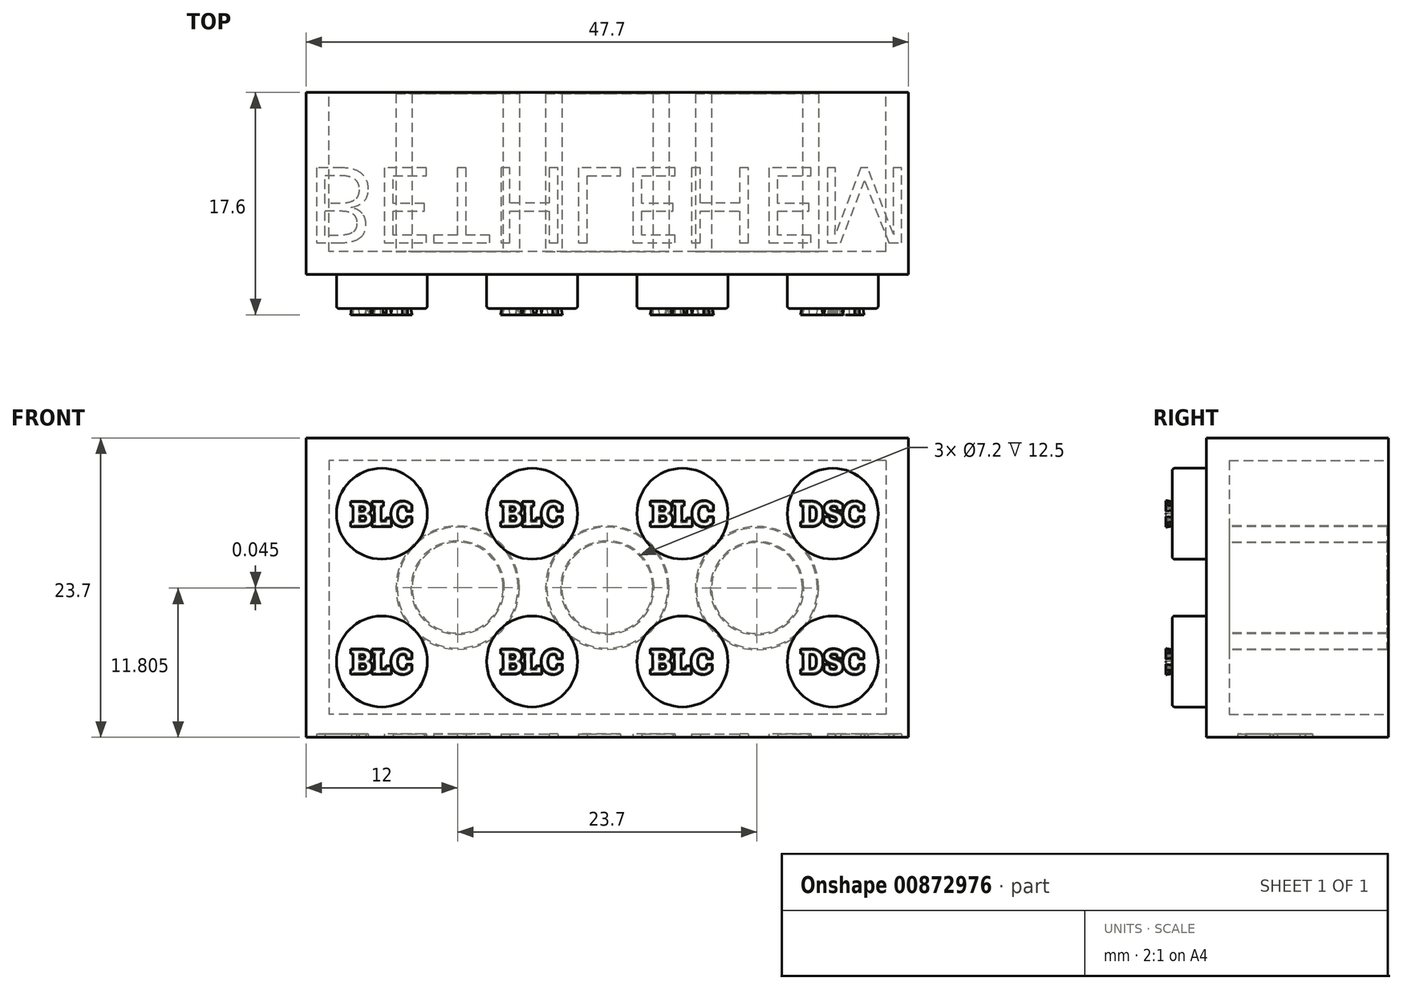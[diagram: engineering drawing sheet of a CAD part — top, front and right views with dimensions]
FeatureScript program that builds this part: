
annotation { "Feature Type Name" : "Feature", "Feature Type Description" : "" }
export const myFeature = defineFeature(function(context is Context, id is Id, definition is map)
    precondition{}
    {
        {
            var Q0;
            Q0=qCreatedBy(makeId("Front.planeOp"),FACE);
            var sketch = newSketch(context, id + "F0", { "sketchPlane" : qUnion([Q0])});
            skLineSegment(sketch, "E0.bottom", {"start": v(-23.85, 11.85) * mm, "end": v(23.85, 11.85) * mm});
            skLineSegment(sketch, "E0.top", {"start": v(-23.85, -11.85) * mm, "end": v(23.85, -11.85) * mm});
            skLineSegment(sketch, "E0.left", {"start": v(-23.85, 11.85) * mm, "end": v(-23.85, -11.85) * mm});
            skLineSegment(sketch, "E0.right", {"start": v(23.85, 11.85) * mm, "end": v(23.85, -11.85) * mm});
            skSolve(sketch);
        }
        {
            var Q0;
            Q0=makeQuery(id+"F0.imprint","IMPRINT",FACE,{"disambiguationData":[TD([[makeQuery(id+"F0.imprint","IMPRINT",EDGE,{"derivedFrom":sQuery(id+"F0.wireOp",EDGE,"E0.bottom")}),-1.0]])]});
            extrude(context, id + "F1", {"entities" : qUnion([Q0]), "depth" : 14.4 * mm, "offsetDistance" : 25 * mm});
        }
        {
            var Q0;
            Q0=makeQuery(id+"F1.opExtrude","CAP_FACE",FACE,{"disambiguationData":[OSD([sQuery(id+"F0.wireOp",EDGE,"E0.bottom"),sQuery(id+"F0.wireOp",EDGE,"E0.top"),sQuery(id+"F0.wireOp",EDGE,"E0.left"),sQuery(id+"F0.wireOp",EDGE,"E0.right")])],"isStart":true});
            var sketch = newSketch(context, id + "F2", { "sketchPlane" : qUnion([Q0])});
            skLineSegment(sketch, "E1.bottom", {"start": v(-22.05, 10.05) * mm, "end": v(22.05, 10.05) * mm});
            skLineSegment(sketch, "E1.top", {"start": v(-22.05, -10.05) * mm, "end": v(22.05, -10.05) * mm});
            skLineSegment(sketch, "E1.left", {"start": v(-22.05, 10.05) * mm, "end": v(-22.05, -10.05) * mm});
            skLineSegment(sketch, "E1.right", {"start": v(22.05, 10.05) * mm, "end": v(22.05, -10.05) * mm});
            skSolve(sketch);
        }
        {
            var Q0;
            Q0=makeQuery(id+"F2.imprint","IMPRINT",FACE,{"disambiguationData":[TD([[makeQuery(id+"F2.imprint","IMPRINT",EDGE,{"derivedFrom":sQuery(id+"F2.wireOp",EDGE,"E1.bottom")}),-1.0]])]});
            extrude(context, id + "F3", {"entities" : qUnion([Q0]), "operationType" : NewBodyOperationType.REMOVE, "oppositeDirection" : true, "depth" : 12.6 * mm, "offsetDistance" : 25 * mm});
        }
        {
            var Q0;
            Q0=makeQuery(id+"F1.opExtrude","CAP_FACE",FACE,{"disambiguationData":[OSD([sQuery(id+"F0.wireOp",EDGE,"E0.bottom"),sQuery(id+"F0.wireOp",EDGE,"E0.top"),sQuery(id+"F0.wireOp",EDGE,"E0.left"),sQuery(id+"F0.wireOp",EDGE,"E0.right")])],"isStart":false});
            var sketch = newSketch(context, id + "F4", { "sketchPlane" : qUnion([Q0])});
            skCircle(sketch, "E2", {"center": v(-17.85, 5.85) * mm, "radius": 3.6 * mm});
            skCircle(sketch, "E3.1.0.0", {"center": v(-5.95, 5.85) * mm, "radius": 3.6 * mm});
            skCircle(sketch, "E3.2.0.0", {"center": v(5.95, 5.85) * mm, "radius": 3.6 * mm});
            skCircle(sketch, "E3.3.0.0", {"center": v(17.85, 5.85) * mm, "radius": 3.6 * mm});
            skLineSegment(sketch, "E3.direction1", {"start": v(-17.85, 5.85) * mm, "end": v(-5.95, 5.85) * mm, "construction": true});
            skCircle(sketch, "E4", {"center": v(-17.85, -5.85) * mm, "radius": 3.6 * mm});
            skCircle(sketch, "E5.1.0.0", {"center": v(-5.95, -5.85) * mm, "radius": 3.6 * mm});
            skCircle(sketch, "E5.2.0.0", {"center": v(5.95, -5.85) * mm, "radius": 3.6 * mm});
            skLineSegment(sketch, "E5.direction1", {"start": v(-17.85, -5.85) * mm, "end": v(-5.95, -5.85) * mm, "construction": true});
            skCircle(sketch, "E6.0.3.0", {"center": v(17.85, -5.85) * mm, "radius": 3.6 * mm});
            skSolve(sketch);
        }
        {
            var Q0;
            Q0=makeQuery(id+"F4.imprint","IMPRINT",FACE,{"disambiguationData":[TD([[makeQuery(id+"F4.imprint","IMPRINT",EDGE,{"derivedFrom":sQuery(id+"F4.wireOp",EDGE,"E2")}),1.0]])]});
            var Q1;
            Q1=makeQuery(id+"F4.imprint","IMPRINT",FACE,{"disambiguationData":[TD([[makeQuery(id+"F4.imprint","IMPRINT",EDGE,{"derivedFrom":sQuery(id+"F4.wireOp",EDGE,"E3.1.0.0")}),1.0]])]});
            var Q2;
            Q2=makeQuery(id+"F4.imprint","IMPRINT",FACE,{"disambiguationData":[TD([[makeQuery(id+"F4.imprint","IMPRINT",EDGE,{"derivedFrom":sQuery(id+"F4.wireOp",EDGE,"E3.2.0.0")}),1.0]])]});
            var Q3;
            Q3=makeQuery(id+"F4.imprint","IMPRINT",FACE,{"disambiguationData":[TD([[makeQuery(id+"F4.imprint","IMPRINT",EDGE,{"derivedFrom":sQuery(id+"F4.wireOp",EDGE,"E3.3.0.0")}),1.0]])]});
            var Q4;
            Q4=makeQuery(id+"F4.imprint","IMPRINT",FACE,{"disambiguationData":[TD([[makeQuery(id+"F4.imprint","IMPRINT",EDGE,{"derivedFrom":sQuery(id+"F4.wireOp",EDGE,"E4")}),1.0]])]});
            var Q5;
            Q5=makeQuery(id+"F4.imprint","IMPRINT",FACE,{"disambiguationData":[TD([[makeQuery(id+"F4.imprint","IMPRINT",EDGE,{"derivedFrom":sQuery(id+"F4.wireOp",EDGE,"E5.1.0.0")}),1.0]])]});
            var Q6;
            Q6=makeQuery(id+"F4.imprint","IMPRINT",FACE,{"disambiguationData":[TD([[makeQuery(id+"F4.imprint","IMPRINT",EDGE,{"derivedFrom":sQuery(id+"F4.wireOp",EDGE,"E5.2.0.0")}),1.0]])]});
            var Q7;
            Q7=makeQuery(id+"F4.imprint","IMPRINT",FACE,{"disambiguationData":[TD([[makeQuery(id+"F4.imprint","IMPRINT",EDGE,{"derivedFrom":sQuery(id+"F4.wireOp",EDGE,"E6.0.3.0")}),1.0]])]});
            extrude(context, id + "F5", {"entities" : qUnion([Q0, Q1, Q2, Q3, Q4, Q5, Q6, Q7]), "depth" : 2.7 * mm, "offsetDistance" : 25 * mm});
        }
        {
            var Q0;
            Q0=makeQuery(id+"F5.opExtrude","CAP_FACE",FACE,{"disambiguationData":[OSD([sQuery(id+"F4.wireOp",EDGE,"E2")])],"isStart":false});
            var sketch = newSketch(context, id + "F6", { "sketchPlane" : qUnion([Q0])});
            skText(sketch, "E7", { "text": "BLC", "fontName": "RobotoSlab-Bold.ttf"});
            skPoint(sketch, "E8", {"position": v(-17.85, 5.85) * mm});
            skText(sketch, "E9", { "text": "BLC", "fontName": "RobotoSlab-Bold.ttf"});
            skPoint(sketch, "E10", {"position": v(-17.85, -5.85) * mm});
            skText(sketch, "E11", { "text": "BLC", "fontName": "RobotoSlab-Bold.ttf"});
            skPoint(sketch, "E12", {"position": v(-5.95, -5.85) * mm});
            skText(sketch, "E13", { "text": "BLC", "fontName": "RobotoSlab-Bold.ttf"});
            skPoint(sketch, "E14", {"position": v(-5.95, 5.85) * mm});
            skText(sketch, "E15", { "text": "BLC", "fontName": "RobotoSlab-Bold.ttf"});
            skPoint(sketch, "E16", {"position": v(5.95, 5.86) * mm});
            skPoint(sketch, "E17", {"position": v(5.95, -5.85) * mm});
            skPoint(sketch, "E18", {"position": v(17.85, 5.82) * mm});
            skText(sketch, "E19", { "text": "DSC", "fontName": "RobotoSlab-Bold.ttf"});
            skPoint(sketch, "E20", {"position": v(17.85, -5.85) * mm});
            skText(sketch, "E21", { "text": "DSC", "fontName": "RobotoSlab-Bold.ttf"});
            skPoint(sketch, "E22", {"position": v(17.85, 5.85) * mm});
            skText(sketch, "E23", { "text": "BLC", "fontName": "RobotoSlab-Bold.ttf"});
            skPoint(sketch, "E24", {"position": v(5.89, -5.85) * mm});
            const initialGuessF6  = {"E7": [-0.02032, 0.00492, 1, 0, 0.00185], "E9": [-0.02032, -0.00678, 1, 0, 0.00185], "E11": [-0.00842, -0.00678, 1, 0, 0.00185], "E13": [-0.00842, 0.00492, 1, 0, 0.00185], "E15": [0.00342, 0.0049, 1, 0, 0.0019], "E19": [0.01532, -0.00678, 1, 0, 0.00186], "E21": [0.01532, 0.00492, 1, 0, 0.00186], "E23": [0.00342, -0.00678, 1, 0, 0.00186]};
            skSetInitialGuess(sketch, initialGuessF6);
            skSolve(sketch);
        }
        {
            var Q0;
            Q0=qSketchRegion(id+"F6",true);
            extrude(context, id + "F7", {"entities" : qUnion([Q0]), "depth" : 0.5 * mm, "offsetDistance" : 25 * mm, "hasDraft" : true, "draftAngle" : 10 * degree});
        }
        {
            var Q0;
            Q0=makeQuery(id+"F5.opExtrude","CAP_EDGE",EDGE,{"disambiguationData":[OSD([sQuery(id+"F4.wireOp",EDGE,"E2")])],"isStart":false});
            var Q1;
            Q1=makeQuery(id+"F5.opExtrude","CAP_EDGE",EDGE,{"disambiguationData":[OSD([sQuery(id+"F4.wireOp",EDGE,"E3.1.0.0")])],"isStart":false});
            var Q2;
            Q2=makeQuery(id+"F5.opExtrude","CAP_EDGE",EDGE,{"disambiguationData":[OSD([sQuery(id+"F4.wireOp",EDGE,"E3.2.0.0")])],"isStart":false});
            var Q3;
            Q3=makeQuery(id+"F5.opExtrude","CAP_EDGE",EDGE,{"disambiguationData":[OSD([sQuery(id+"F4.wireOp",EDGE,"E3.3.0.0")])],"isStart":false});
            var Q4;
            Q4=makeQuery(id+"F5.opExtrude","CAP_EDGE",EDGE,{"disambiguationData":[OSD([sQuery(id+"F4.wireOp",EDGE,"E6.0.3.0")])],"isStart":false});
            var Q5;
            Q5=makeQuery(id+"F5.opExtrude","CAP_EDGE",EDGE,{"disambiguationData":[OSD([sQuery(id+"F4.wireOp",EDGE,"E5.2.0.0")])],"isStart":false});
            var Q6;
            Q6=makeQuery(id+"F5.opExtrude","CAP_EDGE",EDGE,{"disambiguationData":[OSD([sQuery(id+"F4.wireOp",EDGE,"E5.1.0.0")])],"isStart":false});
            var Q7;
            Q7=makeQuery(id+"F5.opExtrude","CAP_EDGE",EDGE,{"disambiguationData":[OSD([sQuery(id+"F4.wireOp",EDGE,"E4")])],"isStart":false});
            fillet(context, id + "F8", {"entities" : qUnion([Q0, Q1, Q2, Q3, Q4, Q5, Q6, Q7]), "radius" : 0.2 * mm, "tangentPropagation" : true, "allowEdgeOverflow" : false});
        }
        {
            var Q0;
            Q0=makeQuery(id+"F3.boolean.opBoolean","COPY",FACE,{"derivedFrom":makeQuery(id+"F3.opExtrude","CAP_FACE",FACE,{"disambiguationData":[OSD([sQuery(id+"F2.wireOp",EDGE,"E1.bottom"),sQuery(id+"F2.wireOp",EDGE,"E1.top"),sQuery(id+"F2.wireOp",EDGE,"E1.left"),sQuery(id+"F2.wireOp",EDGE,"E1.right")])],"isStart":false})});
            var sketch = newSketch(context, id + "F9", { "sketchPlane" : qUnion([Q0])});
            skCircle(sketch, "E25", {"center": v(11.85, 0) * mm, "radius": 4.88 * mm});
            skCircle(sketch, "E26", {"center": v(-11.85, -0.04) * mm, "radius": 4.88 * mm});
            skCircle(sketch, "E27", {"center": v(0, 0) * mm, "radius": 4.88 * mm});
            skSolve(sketch);
        }
        {
            var Q0;
            Q0=makeQuery(id+"F9.imprint","IMPRINT",FACE,{"disambiguationData":[TD([[makeQuery(id+"F9.imprint","IMPRINT",EDGE,{"derivedFrom":sQuery(id+"F9.wireOp",EDGE,"E26")}),1.0]])]});
            var Q1;
            Q1=makeQuery(id+"F9.imprint","IMPRINT",FACE,{"disambiguationData":[TD([[makeQuery(id+"F9.imprint","IMPRINT",EDGE,{"derivedFrom":sQuery(id+"F9.wireOp",EDGE,"E27")}),1.0]])]});
            var Q2;
            Q2=makeQuery(id+"F9.imprint","IMPRINT",FACE,{"disambiguationData":[TD([[makeQuery(id+"F9.imprint","IMPRINT",EDGE,{"derivedFrom":sQuery(id+"F9.wireOp",EDGE,"E25")}),1.0]])]});
            extrude(context, id + "F10", {"entities" : qUnion([Q0, Q1, Q2]), "operationType" : NewBodyOperationType.ADD, "depth" : 12.6 * mm, "offsetDistance" : 25 * mm});
        }
        {
            var Q0;
            Q0=makeQuery(id+"F3.boolean.opBoolean","COPY",FACE,{"derivedFrom":makeQuery(id+"F3.opExtrude","CAP_FACE",FACE,{"disambiguationData":[OSD([sQuery(id+"F2.wireOp",EDGE,"E1.bottom"),sQuery(id+"F2.wireOp",EDGE,"E1.top"),sQuery(id+"F2.wireOp",EDGE,"E1.left"),sQuery(id+"F2.wireOp",EDGE,"E1.right")])],"isStart":false})});
            var sketch = newSketch(context, id + "F11", { "sketchPlane" : qUnion([Q0])});
            skPoint(sketch, "E28", {"position": v(-11.85, -0.04) * mm});
            skPoint(sketch, "E29", {"position": v(11.85, 0) * mm});
            skCircle(sketch, "E30", {"center": v(-11.85, -0.04) * mm, "radius": 3.6 * mm});
            skCircle(sketch, "E31", {"center": v(0, 0) * mm, "radius": 3.6 * mm});
            skCircle(sketch, "E32", {"center": v(11.85, 0) * mm, "radius": 3.6 * mm});
            skSolve(sketch);
        }
        {
            var Q0;
            Q0=qSketchRegion(id+"F11",true);
            extrude(context, id + "F12", {"entities" : qUnion([Q0]), "operationType" : NewBodyOperationType.REMOVE, "oppositeDirection" : true, "depth" : -15 * mm, "offsetDistance" : 25 * mm});
        }
        {
            var Q0;
            Q0=makeQuery(id+"F10.opExtrude","CAP_EDGE",EDGE,{"disambiguationData":[OSD([sQuery(id+"F9.wireOp",EDGE,"E26")])],"isStart":false});
            var Q1;
            Q1=makeQuery(id+"F12.boolean.opBoolean","INTERSECT",EDGE,{"derivedFrom":[makeQuery(id+"F10.opExtrude","CAP_FACE",FACE,{"disambiguationData":[OSD([sQuery(id+"F9.wireOp",EDGE,"E26")])],"isStart":false}),makeQuery(id+"F12.opExtrude","SWEPT_FACE",FACE,{"disambiguationData":[OSD([sQuery(id+"F11.wireOp",EDGE,"E30")])]})]});
            var Q2;
            Q2=makeQuery(id+"F10.opExtrude","CAP_EDGE",EDGE,{"disambiguationData":[OSD([sQuery(id+"F9.wireOp",EDGE,"E27")])],"isStart":false});
            var Q3;
            Q3=makeQuery(id+"F12.boolean.opBoolean","INTERSECT",EDGE,{"derivedFrom":[makeQuery(id+"F10.opExtrude","CAP_FACE",FACE,{"disambiguationData":[OSD([sQuery(id+"F9.wireOp",EDGE,"E27")])],"isStart":false}),makeQuery(id+"F12.opExtrude","SWEPT_FACE",FACE,{"disambiguationData":[OSD([sQuery(id+"F11.wireOp",EDGE,"E31")])]})]});
            var Q4;
            Q4=makeQuery(id+"F10.opExtrude","CAP_EDGE",EDGE,{"disambiguationData":[OSD([sQuery(id+"F9.wireOp",EDGE,"E25")])],"isStart":false});
            var Q5;
            Q5=makeQuery(id+"F12.boolean.opBoolean","INTERSECT",EDGE,{"derivedFrom":[makeQuery(id+"F10.opExtrude","CAP_FACE",FACE,{"disambiguationData":[OSD([sQuery(id+"F9.wireOp",EDGE,"E25")])],"isStart":false}),makeQuery(id+"F12.opExtrude","SWEPT_FACE",FACE,{"disambiguationData":[OSD([sQuery(id+"F11.wireOp",EDGE,"E32")])]})]});
            var Q6;
            Q6=makeQuery(id+"F3.boolean.opBoolean","COPY",EDGE,{"derivedFrom":makeQuery(id+"F3.opExtrude","CAP_EDGE",EDGE,{"disambiguationData":[OSD([sQuery(id+"F2.wireOp",EDGE,"E1.bottom")])],"isStart":true})});
            var Q7;
            Q7=makeQuery(id+"F3.boolean.opBoolean","COPY",EDGE,{"derivedFrom":makeQuery(id+"F3.opExtrude","CAP_EDGE",EDGE,{"disambiguationData":[OSD([sQuery(id+"F2.wireOp",EDGE,"E1.right")])],"isStart":true})});
            var Q8;
            Q8=makeQuery(id+"F3.boolean.opBoolean","COPY",EDGE,{"derivedFrom":makeQuery(id+"F3.opExtrude","CAP_EDGE",EDGE,{"disambiguationData":[OSD([sQuery(id+"F2.wireOp",EDGE,"E1.top")])],"isStart":true})});
            var Q9;
            Q9=makeQuery(id+"F3.boolean.opBoolean","COPY",EDGE,{"derivedFrom":makeQuery(id+"F3.opExtrude","CAP_EDGE",EDGE,{"disambiguationData":[OSD([sQuery(id+"F2.wireOp",EDGE,"E1.left")])],"isStart":true})});
            chamfer(context, id + "F13", {"entities" : qUnion([Q0, Q1, Q2, Q3, Q4, Q5, Q6, Q7, Q8, Q9]), "width" : 0.1 * mm, "tangentPropagation" : true});
        }
        {
            var Q0;
            Q0=makeQuery(id+"F1.opExtrude","SWEPT_FACE",FACE,{"disambiguationData":[OSD([sQuery(id+"F0.wireOp",EDGE,"E0.top")])]});
            var sketch = newSketch(context, id + "F14", { "sketchPlane" : qUnion([Q0])});
            skText(sketch, "E33", { "text": "BETHLEHEM", "fontName": "OpenSans-Regular.ttf"});
            const initialGuessF14  = {"E33": [-0.02385, 0.00597, 1, 0, 0.00599]};
            skSetInitialGuess(sketch, initialGuessF14);
            skSolve(sketch);
        }
        {
            var Q0;
            Q0 = qSketchRegion(id + "F14", true);
            extrude(context, id + "F15", {"entities" : qUnion([Q0]), "operationType" : NewBodyOperationType.REMOVE, "oppositeDirection" : true, "depth" : 0.27 * mm, "offsetDistance" : 25 * mm});
        }
    });
